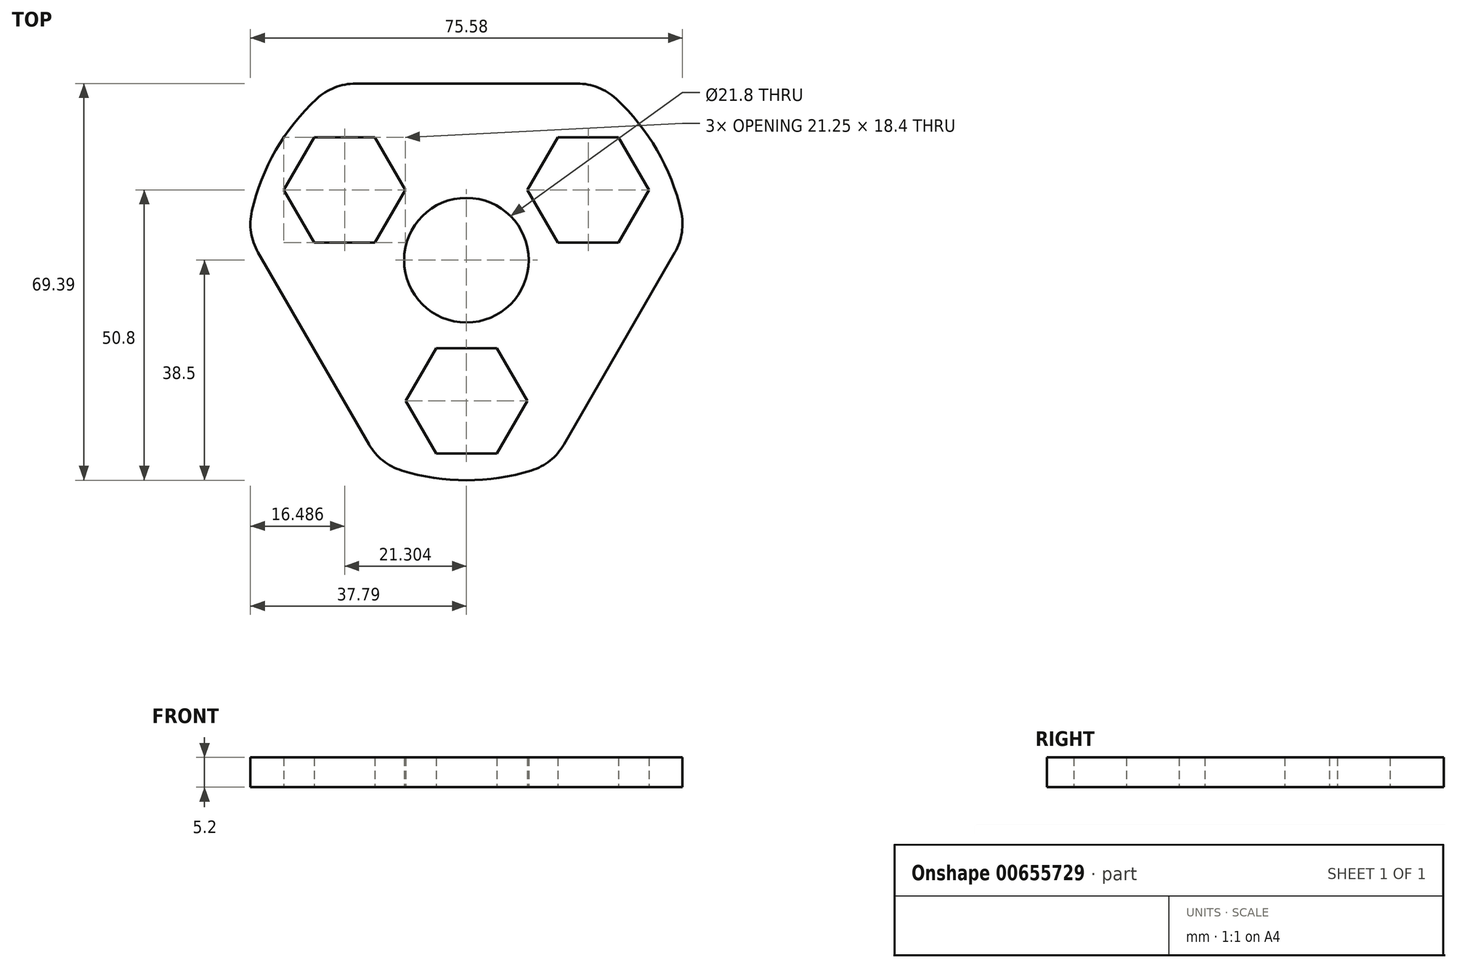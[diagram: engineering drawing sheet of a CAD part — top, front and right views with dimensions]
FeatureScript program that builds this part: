
annotation { "Feature Type Name" : "Feature", "Feature Type Description" : "" }
export const myFeature = defineFeature(function(context is Context, id is Id, definition is map)
    precondition{}
    {
        {
            var Q0;
            Q0=qCreatedBy(makeId("Top.planeOp"),FACE);
            var sketch = newSketch(context, id + "F0", { "sketchPlane" : qUnion([Q0])});
            skArc(sketch, "E0", {"start": v(38.24, 4.45) * mm, "mid": v(33.34, 19.25) * mm, "end": v(22.98, 30.9) * mm});
            skCircle(sketch, "E1", {"center": v(0, 0) * mm, "radius": 10.9 * mm});
            skLineSegment(sketch, "E2", {"start": v(0, 0) * mm, "end": v(0, -24.6) * mm, "construction": true});
            skCircle(sketch, "E3.cCircle", {"center": v(0, -24.6) * mm, "radius": 9.2 * mm, "construction": true});
            skLineSegment(sketch, "E3.0", {"start": v(5.31, -15.4) * mm, "end": v(10.62, -24.6) * mm});
            skLineSegment(sketch, "E3.1", {"start": v(10.62, -24.6) * mm, "end": v(5.31, -33.8) * mm});
            skLineSegment(sketch, "E3.2", {"start": v(5.31, -33.8) * mm, "end": v(-5.31, -33.8) * mm});
            skLineSegment(sketch, "E3.3", {"start": v(-5.31, -33.8) * mm, "end": v(-10.62, -24.6) * mm});
            skLineSegment(sketch, "E3.4", {"start": v(-10.62, -24.6) * mm, "end": v(-5.31, -15.4) * mm});
            skLineSegment(sketch, "E3.5", {"start": v(-5.31, -15.4) * mm, "end": v(5.31, -15.4) * mm});
            skPoint(sketch, "E3.0.midPoint", {"position": v(7.97, -20) * mm});
            skLineSegment(sketch, "E4", {"start": v(0, 0) * mm, "end": v(30, 0) * mm, "construction": true});
            skLineSegment(sketch, "E5", {"start": v(0, 0) * mm, "end": v(-15.26, -35.35) * mm, "construction": true});
            skLineSegment(sketch, "E6", {"start": v(0, 0) * mm, "end": v(15.26, -35.35) * mm, "construction": true});
            skLineSegment(sketch, "E7.1.0", {"start": v(-31.93, 12.3) * mm, "end": v(-26.62, 21.5) * mm});
            skLineSegment(sketch, "E7.1.1", {"start": v(-26.62, 3.1) * mm, "end": v(-31.93, 12.3) * mm});
            skLineSegment(sketch, "E7.1.2", {"start": v(-16, 3.1) * mm, "end": v(-26.62, 3.1) * mm});
            skLineSegment(sketch, "E7.1.3", {"start": v(-10.68, 12.3) * mm, "end": v(-16, 3.1) * mm});
            skLineSegment(sketch, "E7.1.4", {"start": v(-16, 21.5) * mm, "end": v(-10.68, 12.3) * mm});
            skLineSegment(sketch, "E7.1.5", {"start": v(-26.62, 21.5) * mm, "end": v(-16, 21.5) * mm});
            skLineSegment(sketch, "E7.1.6", {"start": v(0, 0) * mm, "end": v(-22.98, 30.9) * mm, "construction": true});
            skLineSegment(sketch, "E7.1.7", {"start": v(0, 0) * mm, "end": v(-38.24, 4.45) * mm, "construction": true});
            skLineSegment(sketch, "E7.2.0", {"start": v(26.62, 21.5) * mm, "end": v(31.93, 12.3) * mm});
            skLineSegment(sketch, "E7.2.1", {"start": v(16, 21.5) * mm, "end": v(26.62, 21.5) * mm});
            skLineSegment(sketch, "E7.2.2", {"start": v(10.68, 12.3) * mm, "end": v(16, 21.5) * mm});
            skLineSegment(sketch, "E7.2.3", {"start": v(16, 3.1) * mm, "end": v(10.68, 12.3) * mm});
            skLineSegment(sketch, "E7.2.4", {"start": v(26.62, 3.1) * mm, "end": v(16, 3.1) * mm});
            skLineSegment(sketch, "E7.2.5", {"start": v(31.93, 12.3) * mm, "end": v(26.62, 3.1) * mm});
            skLineSegment(sketch, "E7.2.6", {"start": v(0, 0) * mm, "end": v(38.24, 4.45) * mm, "construction": true});
            skLineSegment(sketch, "E7.2.7", {"start": v(0, 0) * mm, "end": v(22.98, 30.9) * mm, "construction": true});
            skLineSegment(sketch, "E7.anchor1", {"start": v(0, 0) * mm, "end": v(-5.31, -33.8) * mm, "construction": true});
            skLineSegment(sketch, "E7.anchor2", {"start": v(0, 0) * mm, "end": v(31.93, 12.3) * mm, "construction": true});
            skLineSegment(sketch, "E8", {"start": v(15.26, -35.35) * mm, "end": v(38.24, 4.45) * mm, "construction": true});
            skLineSegment(sketch, "E9", {"start": v(26.75, -15.45) * mm, "end": v(0, 0) * mm, "construction": true});
            skPoint(sketch, "E10", {"position": v(20.78, -12) * mm});
            skArc(sketch, "E11", {"start": v(38.24, 4.45) * mm, "mid": v(20.78, -12) * mm, "end": v(15.26, -35.35) * mm, "construction": true});
            skArc(sketch, "E12.1.0", {"start": v(-15.26, -35.35) * mm, "mid": v(-20.78, -12) * mm, "end": v(-38.24, 4.45) * mm, "construction": true});
            skArc(sketch, "E12.2.0", {"start": v(-22.98, 30.9) * mm, "mid": v(0, 24) * mm, "end": v(22.98, 30.9) * mm, "construction": true});
            skArc(sketch, "E13.trimOffspring", {"start": v(-22.98, 30.9) * mm, "mid": v(-33.34, 19.25) * mm, "end": v(-38.24, 4.45) * mm});
            skArc(sketch, "E14.trimOffspring", {"start": v(-15.26, -35.35) * mm, "mid": v(0, -38.5) * mm, "end": v(15.26, -35.35) * mm});
            skLineSegment(sketch, "E15", {"start": v(38.24, 4.45) * mm, "end": v(15.26, -35.35) * mm});
            skLineSegment(sketch, "E16", {"start": v(-15.26, -35.35) * mm, "end": v(-38.24, 4.45) * mm});
            skLineSegment(sketch, "E17", {"start": v(-22.98, 30.9) * mm, "end": v(22.98, 30.9) * mm});
            skSolve(sketch);
        }
        {
            var Q0;
            Q0=makeQuery(id+"F0.imprint","IMPRINT",FACE,{"disambiguationData":[TD([[makeQuery(id+"F0.imprint","IMPRINT",EDGE,{"derivedFrom":sQuery(id+"F0.wireOp",EDGE,"E0")}),1.0]])]});
            extrude(context, id + "F1", {"entities" : qUnion([Q0]), "depth" : 5.2 * mm, "offsetDistance" : 25 * mm});
        }
        {
            var Q0;
            Q0=makeQuery(id+"F1.opExtrude","SWEPT_EDGE",EDGE,{"disambiguationData":[OSD([sQuery(id+"F0.wireOp",EDGE,"E12.1.0"),sQuery(id+"F0.wireOp",EDGE,"E13.trimOffspring")])]});
            var Q1;
            Q1=makeQuery(id+"F1.opExtrude","SWEPT_EDGE",EDGE,{"disambiguationData":[OSD([sQuery(id+"F0.wireOp",EDGE,"E12.2.0"),sQuery(id+"F0.wireOp",EDGE,"E13.trimOffspring")])]});
            var Q2;
            Q2=makeQuery(id+"F1.opExtrude","SWEPT_EDGE",EDGE,{"disambiguationData":[OSD([sQuery(id+"F0.wireOp",EDGE,"E0"),sQuery(id+"F0.wireOp",EDGE,"E12.2.0")])]});
            var Q3;
            Q3=makeQuery(id+"F1.opExtrude","SWEPT_EDGE",EDGE,{"disambiguationData":[OSD([sQuery(id+"F0.wireOp",EDGE,"E0"),sQuery(id+"F0.wireOp",EDGE,"E11")])]});
            var Q4;
            Q4=makeQuery(id+"F1.opExtrude","SWEPT_EDGE",EDGE,{"disambiguationData":[OSD([sQuery(id+"F0.wireOp",EDGE,"E11"),sQuery(id+"F0.wireOp",EDGE,"E14.trimOffspring")])]});
            var Q5;
            Q5=makeQuery(id+"F1.opExtrude","SWEPT_EDGE",EDGE,{"disambiguationData":[OSD([sQuery(id+"F0.wireOp",EDGE,"E12.1.0"),sQuery(id+"F0.wireOp",EDGE,"E14.trimOffspring")])]});
            fillet(context, id + "F2", {"entities" : qUnion([Q0, Q1, Q2, Q3, Q4, Q5]), "radius" : 10 * mm, "tangentPropagation" : true, "allowEdgeOverflow" : false});
        }
    });
